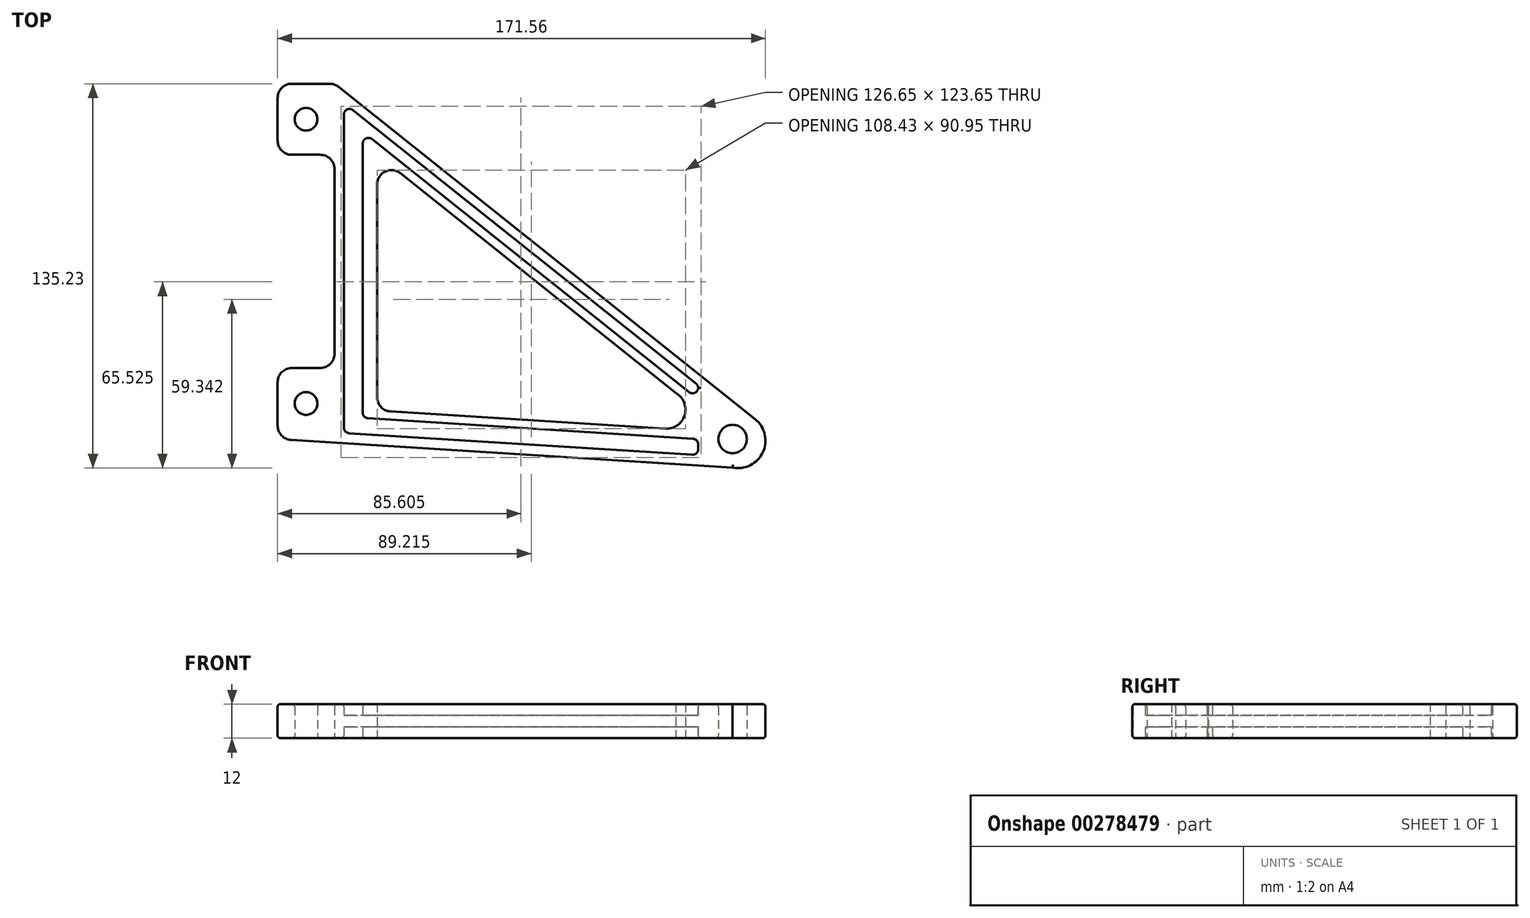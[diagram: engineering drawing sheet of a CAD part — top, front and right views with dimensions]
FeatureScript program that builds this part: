
annotation { "Feature Type Name" : "Feature", "Feature Type Description" : "" }
export const myFeature = defineFeature(function(context is Context, id is Id, definition is map)
    precondition{}
    {
        {
            var Q0;
            Q0=qCreatedBy(makeId("Top.planeOp"),FACE);
            var sketch = newSketch(context, id + "F0", { "sketchPlane" : qUnion([Q0])});
            skCircle(sketch, "E0", {"center": v(0, 0) * mm, "radius": 5 * mm});
            skCircle(sketch, "E1", {"center": v(-150, 12.5) * mm, "radius": 4 * mm});
            skCircle(sketch, "E2", {"center": v(-150, 112.5) * mm, "radius": 4 * mm});
            skLineSegment(sketch, "E3", {"start": v(0, -10.05) * mm, "end": v(-160, 0) * mm});
            skLineSegment(sketch, "E4", {"start": v(-160, 0) * mm, "end": v(-160, 25) * mm});
            skLineSegment(sketch, "E5", {"start": v(-160, 25) * mm, "end": v(-140, 25) * mm});
            skLineSegment(sketch, "E6", {"start": v(-140, 25) * mm, "end": v(-140, 100) * mm});
            skLineSegment(sketch, "E7", {"start": v(-140, 100) * mm, "end": v(-160, 100) * mm});
            skLineSegment(sketch, "E8", {"start": v(-160, 100) * mm, "end": v(-160, 125) * mm});
            skLineSegment(sketch, "E9", {"start": v(-125, 100) * mm, "end": v(-125, 10) * mm});
            skLineSegment(sketch, "E10", {"start": v(-125, 10) * mm, "end": v(-23.73, 3.64) * mm});
            skLineSegment(sketch, "E11", {"start": v(-20.03, 16.27) * mm, "end": v(-125, 100) * mm});
            skLineSegment(sketch, "E12", {"start": v(-160, 125) * mm, "end": v(-140, 125) * mm});
            skLineSegment(sketch, "E13", {"start": v(-140, 125) * mm, "end": v(7.92, 7.02) * mm});
            skArc(sketch, "E14", {"start": v(7.92, 7.02) * mm, "mid": v(10.66, -4.62) * mm, "end": v(0, -10.05) * mm});
            skArc(sketch, "E15", {"start": v(-23.73, 3.64) * mm, "mid": v(-16.83, 8.47) * mm, "end": v(-20.03, 16.27) * mm});
            skLineSegment(sketch, "E16", {"start": v(-136.72, 113) * mm, "end": v(-136.72, 2.16) * mm});
            skLineSegment(sketch, "E17", {"start": v(-136.72, 2.16) * mm, "end": v(-12.07, -5.67) * mm});
            skLineSegment(sketch, "E18", {"start": v(-12.07, -5.67) * mm, "end": v(-12.07, 0) * mm});
            skLineSegment(sketch, "E19", {"start": v(-12.07, 0) * mm, "end": v(-130.08, 7.41) * mm});
            skLineSegment(sketch, "E20", {"start": v(-130.08, 7.41) * mm, "end": v(-130.08, 108.08) * mm});
            skLineSegment(sketch, "E21", {"start": v(-130.08, 108.08) * mm, "end": v(-12.07, 13.96) * mm});
            skLineSegment(sketch, "E22", {"start": v(-12.07, 13.96) * mm, "end": v(-12.07, 18.87) * mm});
            skLineSegment(sketch, "E23", {"start": v(-12.07, 18.87) * mm, "end": v(-136.72, 118.3) * mm});
            skLineSegment(sketch, "E24", {"start": v(-136.72, 118.3) * mm, "end": v(-136.72, 113) * mm});
            skSolve(sketch);
        }
        {
            var Q0;
            Q0=makeQuery(id+"F0.imprint","IMPRINT",FACE,{"disambiguationData":[TD([[makeQuery(id+"F0.imprint","IMPRINT",EDGE,{"derivedFrom":sQuery(id+"F0.wireOp",EDGE,"E0")}),-1.0]])]});
            extrude(context, id + "F1", {"entities" : qUnion([Q0]), "depth" : 12 * mm});
        }
        {
            var Q0;
            Q0=makeQuery(id+"F1.opExtrude","SWEPT_EDGE",EDGE,{"disambiguationData":[OSD([sQuery(id+"F0.wireOp",EDGE,"E5"),sQuery(id+"F0.wireOp",EDGE,"E6")])]});
            var Q1;
            Q1=makeQuery(id+"F1.opExtrude","SWEPT_EDGE",EDGE,{"disambiguationData":[OSD([sQuery(id+"F0.wireOp",EDGE,"E6"),sQuery(id+"F0.wireOp",EDGE,"E7")])]});
            var Q2;
            Q2=makeQuery(id+"F1.opExtrude","SWEPT_EDGE",EDGE,{"disambiguationData":[OSD([sQuery(id+"F0.wireOp",EDGE,"E9"),sQuery(id+"F0.wireOp",EDGE,"E10")])]});
            var Q3;
            Q3=makeQuery(id+"F1.opExtrude","SWEPT_EDGE",EDGE,{"disambiguationData":[OSD([sQuery(id+"F0.wireOp",EDGE,"E9"),sQuery(id+"F0.wireOp",EDGE,"E11")])]});
            var Q4;
            Q4=makeQuery(id+"F1.opExtrude","SWEPT_EDGE",EDGE,{"disambiguationData":[OSD([sQuery(id+"F0.wireOp",EDGE,"E4"),sQuery(id+"F0.wireOp",EDGE,"E5")])]});
            var Q5;
            Q5=makeQuery(id+"F1.opExtrude","SWEPT_EDGE",EDGE,{"disambiguationData":[OSD([sQuery(id+"F0.wireOp",EDGE,"E3"),sQuery(id+"F0.wireOp",EDGE,"E4")])]});
            var Q6;
            Q6=makeQuery(id+"F1.opExtrude","SWEPT_EDGE",EDGE,{"disambiguationData":[OSD([sQuery(id+"F0.wireOp",EDGE,"E7"),sQuery(id+"F0.wireOp",EDGE,"E8")])]});
            var Q7;
            Q7=makeQuery(id+"F1.opExtrude","SWEPT_EDGE",EDGE,{"disambiguationData":[OSD([sQuery(id+"F0.wireOp",EDGE,"E8"),sQuery(id+"F0.wireOp",EDGE,"E12")])]});
            var Q8;
            Q8=makeQuery(id+"F1.opExtrude","SWEPT_EDGE",EDGE,{"disambiguationData":[OSD([sQuery(id+"F0.wireOp",EDGE,"E12"),sQuery(id+"F0.wireOp",EDGE,"E13")])]});
            fillet(context, id + "F2", {"entities" : qUnion([Q0, Q1, Q2, Q3, Q4, Q5, Q6, Q7, Q8]), "radius" : 5 * mm, "tangentPropagation" : true, "allowEdgeOverflow" : false});
        }
        {
            var Q0;
            Q0=makeQuery(id+"F0.imprint","IMPRINT",FACE,{"disambiguationData":[TD([[makeQuery(id+"F0.imprint","IMPRINT",EDGE,{"derivedFrom":sQuery(id+"F0.wireOp",EDGE,"E16")}),1.0]])]});
            extrude(context, id + "F3", {"entities" : qUnion([Q0]), "operationType" : NewBodyOperationType.ADD, "depth" : 8 * mm, "hasSecondDirection" : true, "secondDirectionOppositeDirection" : false, "secondDirectionDepth" : 4 * mm});
        }
        {
            var Q0;
            {var subQ0=sQuery(id+"F0.wireOp",EDGE,"E24");var subQ1=sQuery(id+"F0.wireOp",EDGE,"E23");var subQ2=sQuery(id+"F0.wireOp",EDGE,"E22");var subQ3=sQuery(id+"F0.wireOp",EDGE,"E21");var subQ4=sQuery(id+"F0.wireOp",EDGE,"E20");var subQ5=sQuery(id+"F0.wireOp",EDGE,"E19");var subQ6=sQuery(id+"F0.wireOp",EDGE,"E18");var subQ7=sQuery(id+"F0.wireOp",EDGE,"E17");var subQ8=sQuery(id+"F0.wireOp",EDGE,"E16");Q0=makeQuery(id+"F3.boolean.opBoolean","SPLIT",EDGE,{"disambiguationData":[TD([makeQuery(id+"F3.opExtrude","CAP_FACE",FACE,{"disambiguationData":[OSD([subQ8,subQ7,subQ6,subQ5,subQ4,subQ3,subQ2,subQ1,subQ0])],"isStart":false})])],"derivedFrom":makeQuery(id+"F1.opExtrude","SWEPT_EDGE",EDGE,{"disambiguationData":[OSD([subQ1,subQ0])]})});}
            var Q1;
            {var subQ0=sQuery(id+"F0.wireOp",EDGE,"E24");var subQ1=sQuery(id+"F0.wireOp",EDGE,"E23");var subQ2=sQuery(id+"F0.wireOp",EDGE,"E22");var subQ3=sQuery(id+"F0.wireOp",EDGE,"E21");var subQ4=sQuery(id+"F0.wireOp",EDGE,"E20");var subQ5=sQuery(id+"F0.wireOp",EDGE,"E19");var subQ6=sQuery(id+"F0.wireOp",EDGE,"E18");var subQ7=sQuery(id+"F0.wireOp",EDGE,"E17");var subQ8=sQuery(id+"F0.wireOp",EDGE,"E16");Q1=makeQuery(id+"F3.boolean.opBoolean","SPLIT",EDGE,{"disambiguationData":[TD([makeQuery(id+"F3.opExtrude","CAP_FACE",FACE,{"disambiguationData":[OSD([subQ8,subQ7,subQ6,subQ5,subQ4,subQ3,subQ2,subQ1,subQ0])],"isStart":false})])],"derivedFrom":makeQuery(id+"F1.opExtrude","SWEPT_EDGE",EDGE,{"disambiguationData":[OSD([subQ5,subQ4])]})});}
            var Q2;
            {var subQ0=sQuery(id+"F0.wireOp",EDGE,"E24");var subQ1=sQuery(id+"F0.wireOp",EDGE,"E23");var subQ2=sQuery(id+"F0.wireOp",EDGE,"E22");var subQ3=sQuery(id+"F0.wireOp",EDGE,"E21");var subQ4=sQuery(id+"F0.wireOp",EDGE,"E20");var subQ5=sQuery(id+"F0.wireOp",EDGE,"E19");var subQ6=sQuery(id+"F0.wireOp",EDGE,"E18");var subQ7=sQuery(id+"F0.wireOp",EDGE,"E17");var subQ8=sQuery(id+"F0.wireOp",EDGE,"E16");Q2=makeQuery(id+"F3.boolean.opBoolean","SPLIT",EDGE,{"disambiguationData":[TD([makeQuery(id+"F3.opExtrude","CAP_FACE",FACE,{"disambiguationData":[OSD([subQ8,subQ7,subQ6,subQ5,subQ4,subQ3,subQ2,subQ1,subQ0])],"isStart":false})])],"derivedFrom":makeQuery(id+"F1.opExtrude","SWEPT_EDGE",EDGE,{"disambiguationData":[OSD([subQ8,subQ7])]})});}
            var Q3;
            {var subQ0=sQuery(id+"F0.wireOp",EDGE,"E24");var subQ1=sQuery(id+"F0.wireOp",EDGE,"E23");var subQ2=sQuery(id+"F0.wireOp",EDGE,"E22");var subQ3=sQuery(id+"F0.wireOp",EDGE,"E21");var subQ4=sQuery(id+"F0.wireOp",EDGE,"E20");var subQ5=sQuery(id+"F0.wireOp",EDGE,"E19");var subQ6=sQuery(id+"F0.wireOp",EDGE,"E18");var subQ7=sQuery(id+"F0.wireOp",EDGE,"E17");var subQ8=sQuery(id+"F0.wireOp",EDGE,"E16");Q3=makeQuery(id+"F3.boolean.opBoolean","SPLIT",EDGE,{"disambiguationData":[TD([makeQuery(id+"F3.opExtrude","CAP_FACE",FACE,{"disambiguationData":[OSD([subQ8,subQ7,subQ6,subQ5,subQ4,subQ3,subQ2,subQ1,subQ0])],"isStart":false})])],"derivedFrom":makeQuery(id+"F1.opExtrude","SWEPT_EDGE",EDGE,{"disambiguationData":[OSD([subQ4,subQ3])]})});}
            var Q4;
            {var subQ0=sQuery(id+"F0.wireOp",EDGE,"E24");var subQ1=sQuery(id+"F0.wireOp",EDGE,"E23");var subQ2=sQuery(id+"F0.wireOp",EDGE,"E22");var subQ3=sQuery(id+"F0.wireOp",EDGE,"E21");var subQ4=sQuery(id+"F0.wireOp",EDGE,"E20");var subQ5=sQuery(id+"F0.wireOp",EDGE,"E19");var subQ6=sQuery(id+"F0.wireOp",EDGE,"E18");var subQ7=sQuery(id+"F0.wireOp",EDGE,"E17");var subQ8=sQuery(id+"F0.wireOp",EDGE,"E16");Q4=makeQuery(id+"F3.boolean.opBoolean","SPLIT",EDGE,{"disambiguationData":[TD([makeQuery(id+"F3.opExtrude","CAP_FACE",FACE,{"disambiguationData":[OSD([subQ8,subQ7,subQ6,subQ5,subQ4,subQ3,subQ2,subQ1,subQ0])],"isStart":false})])],"derivedFrom":makeQuery(id+"F1.opExtrude","SWEPT_EDGE",EDGE,{"disambiguationData":[OSD([subQ2,subQ1])]})});}
            var Q5;
            {var subQ0=sQuery(id+"F0.wireOp",EDGE,"E24");var subQ1=sQuery(id+"F0.wireOp",EDGE,"E23");var subQ2=sQuery(id+"F0.wireOp",EDGE,"E22");var subQ3=sQuery(id+"F0.wireOp",EDGE,"E21");var subQ4=sQuery(id+"F0.wireOp",EDGE,"E20");var subQ5=sQuery(id+"F0.wireOp",EDGE,"E19");var subQ6=sQuery(id+"F0.wireOp",EDGE,"E18");var subQ7=sQuery(id+"F0.wireOp",EDGE,"E17");var subQ8=sQuery(id+"F0.wireOp",EDGE,"E16");Q5=makeQuery(id+"F3.boolean.opBoolean","SPLIT",EDGE,{"disambiguationData":[TD([makeQuery(id+"F3.opExtrude","CAP_FACE",FACE,{"disambiguationData":[OSD([subQ8,subQ7,subQ6,subQ5,subQ4,subQ3,subQ2,subQ1,subQ0])],"isStart":false})])],"derivedFrom":makeQuery(id+"F1.opExtrude","SWEPT_EDGE",EDGE,{"disambiguationData":[OSD([subQ7,subQ6])]})});}
            var Q6;
            {var subQ0=sQuery(id+"F0.wireOp",EDGE,"E24");var subQ1=sQuery(id+"F0.wireOp",EDGE,"E23");var subQ2=sQuery(id+"F0.wireOp",EDGE,"E22");var subQ3=sQuery(id+"F0.wireOp",EDGE,"E21");var subQ4=sQuery(id+"F0.wireOp",EDGE,"E20");var subQ5=sQuery(id+"F0.wireOp",EDGE,"E19");var subQ6=sQuery(id+"F0.wireOp",EDGE,"E18");var subQ7=sQuery(id+"F0.wireOp",EDGE,"E17");var subQ8=sQuery(id+"F0.wireOp",EDGE,"E16");Q6=makeQuery(id+"F3.boolean.opBoolean","SPLIT",EDGE,{"disambiguationData":[TD([makeQuery(id+"F3.opExtrude","CAP_FACE",FACE,{"disambiguationData":[OSD([subQ8,subQ7,subQ6,subQ5,subQ4,subQ3,subQ2,subQ1,subQ0])],"isStart":false})])],"derivedFrom":makeQuery(id+"F1.opExtrude","SWEPT_EDGE",EDGE,{"disambiguationData":[OSD([subQ6,subQ5])]})});}
            var Q7;
            {var subQ0=sQuery(id+"F0.wireOp",EDGE,"E24");var subQ1=sQuery(id+"F0.wireOp",EDGE,"E23");var subQ2=sQuery(id+"F0.wireOp",EDGE,"E22");var subQ3=sQuery(id+"F0.wireOp",EDGE,"E21");var subQ4=sQuery(id+"F0.wireOp",EDGE,"E20");var subQ5=sQuery(id+"F0.wireOp",EDGE,"E19");var subQ6=sQuery(id+"F0.wireOp",EDGE,"E18");var subQ7=sQuery(id+"F0.wireOp",EDGE,"E17");var subQ8=sQuery(id+"F0.wireOp",EDGE,"E16");Q7=makeQuery(id+"F3.boolean.opBoolean","SPLIT",EDGE,{"disambiguationData":[TD([makeQuery(id+"F3.opExtrude","CAP_FACE",FACE,{"disambiguationData":[OSD([subQ8,subQ7,subQ6,subQ5,subQ4,subQ3,subQ2,subQ1,subQ0])],"isStart":false})])],"derivedFrom":makeQuery(id+"F1.opExtrude","SWEPT_EDGE",EDGE,{"disambiguationData":[OSD([subQ3,subQ2])]})});}
            var Q8;
            {var subQ0=sQuery(id+"F0.wireOp",EDGE,"E24");var subQ1=sQuery(id+"F0.wireOp",EDGE,"E23");var subQ2=sQuery(id+"F0.wireOp",EDGE,"E22");var subQ3=sQuery(id+"F0.wireOp",EDGE,"E21");var subQ4=sQuery(id+"F0.wireOp",EDGE,"E20");var subQ5=sQuery(id+"F0.wireOp",EDGE,"E19");var subQ6=sQuery(id+"F0.wireOp",EDGE,"E18");var subQ7=sQuery(id+"F0.wireOp",EDGE,"E17");var subQ8=sQuery(id+"F0.wireOp",EDGE,"E16");Q8=makeQuery(id+"F3.boolean.opBoolean","SPLIT",EDGE,{"disambiguationData":[TD([makeQuery(id+"F3.opExtrude","CAP_FACE",FACE,{"disambiguationData":[OSD([subQ8,subQ7,subQ6,subQ5,subQ4,subQ3,subQ2,subQ1,subQ0])],"isStart":true})])],"derivedFrom":makeQuery(id+"F1.opExtrude","SWEPT_EDGE",EDGE,{"disambiguationData":[OSD([subQ1,subQ0])]})});}
            var Q9;
            {var subQ0=sQuery(id+"F0.wireOp",EDGE,"E24");var subQ1=sQuery(id+"F0.wireOp",EDGE,"E23");var subQ2=sQuery(id+"F0.wireOp",EDGE,"E22");var subQ3=sQuery(id+"F0.wireOp",EDGE,"E21");var subQ4=sQuery(id+"F0.wireOp",EDGE,"E20");var subQ5=sQuery(id+"F0.wireOp",EDGE,"E19");var subQ6=sQuery(id+"F0.wireOp",EDGE,"E18");var subQ7=sQuery(id+"F0.wireOp",EDGE,"E17");var subQ8=sQuery(id+"F0.wireOp",EDGE,"E16");Q9=makeQuery(id+"F3.boolean.opBoolean","SPLIT",EDGE,{"disambiguationData":[TD([makeQuery(id+"F3.opExtrude","CAP_FACE",FACE,{"disambiguationData":[OSD([subQ8,subQ7,subQ6,subQ5,subQ4,subQ3,subQ2,subQ1,subQ0])],"isStart":true})])],"derivedFrom":makeQuery(id+"F1.opExtrude","SWEPT_EDGE",EDGE,{"disambiguationData":[OSD([subQ4,subQ3])]})});}
            var Q10;
            {var subQ0=sQuery(id+"F0.wireOp",EDGE,"E24");var subQ1=sQuery(id+"F0.wireOp",EDGE,"E23");var subQ2=sQuery(id+"F0.wireOp",EDGE,"E22");var subQ3=sQuery(id+"F0.wireOp",EDGE,"E21");var subQ4=sQuery(id+"F0.wireOp",EDGE,"E20");var subQ5=sQuery(id+"F0.wireOp",EDGE,"E19");var subQ6=sQuery(id+"F0.wireOp",EDGE,"E18");var subQ7=sQuery(id+"F0.wireOp",EDGE,"E17");var subQ8=sQuery(id+"F0.wireOp",EDGE,"E16");Q10=makeQuery(id+"F3.boolean.opBoolean","SPLIT",EDGE,{"disambiguationData":[TD([makeQuery(id+"F3.opExtrude","CAP_FACE",FACE,{"disambiguationData":[OSD([subQ8,subQ7,subQ6,subQ5,subQ4,subQ3,subQ2,subQ1,subQ0])],"isStart":true})])],"derivedFrom":makeQuery(id+"F1.opExtrude","SWEPT_EDGE",EDGE,{"disambiguationData":[OSD([subQ2,subQ1])]})});}
            var Q11;
            {var subQ0=sQuery(id+"F0.wireOp",EDGE,"E24");var subQ1=sQuery(id+"F0.wireOp",EDGE,"E23");var subQ2=sQuery(id+"F0.wireOp",EDGE,"E22");var subQ3=sQuery(id+"F0.wireOp",EDGE,"E21");var subQ4=sQuery(id+"F0.wireOp",EDGE,"E20");var subQ5=sQuery(id+"F0.wireOp",EDGE,"E19");var subQ6=sQuery(id+"F0.wireOp",EDGE,"E18");var subQ7=sQuery(id+"F0.wireOp",EDGE,"E17");var subQ8=sQuery(id+"F0.wireOp",EDGE,"E16");Q11=makeQuery(id+"F3.boolean.opBoolean","SPLIT",EDGE,{"disambiguationData":[TD([makeQuery(id+"F3.opExtrude","CAP_FACE",FACE,{"disambiguationData":[OSD([subQ8,subQ7,subQ6,subQ5,subQ4,subQ3,subQ2,subQ1,subQ0])],"isStart":true})])],"derivedFrom":makeQuery(id+"F1.opExtrude","SWEPT_EDGE",EDGE,{"disambiguationData":[OSD([subQ3,subQ2])]})});}
            var Q12;
            {var subQ0=sQuery(id+"F0.wireOp",EDGE,"E24");var subQ1=sQuery(id+"F0.wireOp",EDGE,"E23");var subQ2=sQuery(id+"F0.wireOp",EDGE,"E22");var subQ3=sQuery(id+"F0.wireOp",EDGE,"E21");var subQ4=sQuery(id+"F0.wireOp",EDGE,"E20");var subQ5=sQuery(id+"F0.wireOp",EDGE,"E19");var subQ6=sQuery(id+"F0.wireOp",EDGE,"E18");var subQ7=sQuery(id+"F0.wireOp",EDGE,"E17");var subQ8=sQuery(id+"F0.wireOp",EDGE,"E16");Q12=makeQuery(id+"F3.boolean.opBoolean","SPLIT",EDGE,{"disambiguationData":[TD([makeQuery(id+"F3.opExtrude","CAP_FACE",FACE,{"disambiguationData":[OSD([subQ8,subQ7,subQ6,subQ5,subQ4,subQ3,subQ2,subQ1,subQ0])],"isStart":true})])],"derivedFrom":makeQuery(id+"F1.opExtrude","SWEPT_EDGE",EDGE,{"disambiguationData":[OSD([subQ6,subQ5])]})});}
            var Q13;
            {var subQ0=sQuery(id+"F0.wireOp",EDGE,"E24");var subQ1=sQuery(id+"F0.wireOp",EDGE,"E23");var subQ2=sQuery(id+"F0.wireOp",EDGE,"E22");var subQ3=sQuery(id+"F0.wireOp",EDGE,"E21");var subQ4=sQuery(id+"F0.wireOp",EDGE,"E20");var subQ5=sQuery(id+"F0.wireOp",EDGE,"E19");var subQ6=sQuery(id+"F0.wireOp",EDGE,"E18");var subQ7=sQuery(id+"F0.wireOp",EDGE,"E17");var subQ8=sQuery(id+"F0.wireOp",EDGE,"E16");Q13=makeQuery(id+"F3.boolean.opBoolean","SPLIT",EDGE,{"disambiguationData":[TD([makeQuery(id+"F3.opExtrude","CAP_FACE",FACE,{"disambiguationData":[OSD([subQ8,subQ7,subQ6,subQ5,subQ4,subQ3,subQ2,subQ1,subQ0])],"isStart":true})])],"derivedFrom":makeQuery(id+"F1.opExtrude","SWEPT_EDGE",EDGE,{"disambiguationData":[OSD([subQ7,subQ6])]})});}
            var Q14;
            {var subQ0=sQuery(id+"F0.wireOp",EDGE,"E24");var subQ1=sQuery(id+"F0.wireOp",EDGE,"E23");var subQ2=sQuery(id+"F0.wireOp",EDGE,"E22");var subQ3=sQuery(id+"F0.wireOp",EDGE,"E21");var subQ4=sQuery(id+"F0.wireOp",EDGE,"E20");var subQ5=sQuery(id+"F0.wireOp",EDGE,"E19");var subQ6=sQuery(id+"F0.wireOp",EDGE,"E18");var subQ7=sQuery(id+"F0.wireOp",EDGE,"E17");var subQ8=sQuery(id+"F0.wireOp",EDGE,"E16");Q14=makeQuery(id+"F3.boolean.opBoolean","SPLIT",EDGE,{"disambiguationData":[TD([makeQuery(id+"F3.opExtrude","CAP_FACE",FACE,{"disambiguationData":[OSD([subQ8,subQ7,subQ6,subQ5,subQ4,subQ3,subQ2,subQ1,subQ0])],"isStart":true})])],"derivedFrom":makeQuery(id+"F1.opExtrude","SWEPT_EDGE",EDGE,{"disambiguationData":[OSD([subQ5,subQ4])]})});}
            var Q15;
            {var subQ0=sQuery(id+"F0.wireOp",EDGE,"E24");var subQ1=sQuery(id+"F0.wireOp",EDGE,"E23");var subQ2=sQuery(id+"F0.wireOp",EDGE,"E22");var subQ3=sQuery(id+"F0.wireOp",EDGE,"E21");var subQ4=sQuery(id+"F0.wireOp",EDGE,"E20");var subQ5=sQuery(id+"F0.wireOp",EDGE,"E19");var subQ6=sQuery(id+"F0.wireOp",EDGE,"E18");var subQ7=sQuery(id+"F0.wireOp",EDGE,"E17");var subQ8=sQuery(id+"F0.wireOp",EDGE,"E16");Q15=makeQuery(id+"F3.boolean.opBoolean","SPLIT",EDGE,{"disambiguationData":[TD([makeQuery(id+"F3.opExtrude","CAP_FACE",FACE,{"disambiguationData":[OSD([subQ8,subQ7,subQ6,subQ5,subQ4,subQ3,subQ2,subQ1,subQ0])],"isStart":true})])],"derivedFrom":makeQuery(id+"F1.opExtrude","SWEPT_EDGE",EDGE,{"disambiguationData":[OSD([subQ8,subQ7])]})});}
            fillet(context, id + "F4", {"entities" : qUnion([Q0, Q1, Q2, Q3, Q4, Q5, Q6, Q7, Q8, Q9, Q10, Q11, Q12, Q13, Q14, Q15]), "radius" : 2 * mm, "tangentPropagation" : true, "allowEdgeOverflow" : false});
        }
        {
            var Q0;
            Q0=makeQuery(id+"F1.opExtrude","CAP_EDGE",EDGE,{"disambiguationData":[OSD([sQuery(id+"F0.wireOp",EDGE,"E23")])],"isStart":true});
            var Q1;
            Q1=makeQuery(id+"F1.opExtrude","CAP_EDGE",EDGE,{"disambiguationData":[OSD([sQuery(id+"F0.wireOp",EDGE,"E17")])],"isStart":false});
            var Q2;
            Q2=makeQuery(id+"F1.opExtrude","CAP_EDGE",EDGE,{"disambiguationData":[OSD([sQuery(id+"F0.wireOp",EDGE,"E13")])],"isStart":false});
            var Q3;
            Q3=makeQuery(id+"F1.opExtrude","CAP_EDGE",EDGE,{"disambiguationData":[OSD([sQuery(id+"F0.wireOp",EDGE,"E13")])],"isStart":true});
            var Q4;
            Q4=makeQuery(id+"F1.opExtrude","CAP_EDGE",EDGE,{"disambiguationData":[OSD([sQuery(id+"F0.wireOp",EDGE,"E2")])],"isStart":true});
            var Q5;
            Q5=makeQuery(id+"F1.opExtrude","CAP_EDGE",EDGE,{"disambiguationData":[OSD([sQuery(id+"F0.wireOp",EDGE,"E2")])],"isStart":false});
            var Q6;
            Q6=makeQuery(id+"F1.opExtrude","CAP_EDGE",EDGE,{"disambiguationData":[OSD([sQuery(id+"F0.wireOp",EDGE,"E1")])],"isStart":false});
            var Q7;
            Q7=makeQuery(id+"F1.opExtrude","CAP_EDGE",EDGE,{"disambiguationData":[OSD([sQuery(id+"F0.wireOp",EDGE,"E1")])],"isStart":true});
            var Q8;
            Q8=makeQuery(id+"F1.opExtrude","CAP_EDGE",EDGE,{"disambiguationData":[OSD([sQuery(id+"F0.wireOp",EDGE,"E0")])],"isStart":true});
            var Q9;
            Q9=makeQuery(id+"F1.opExtrude","CAP_EDGE",EDGE,{"disambiguationData":[OSD([sQuery(id+"F0.wireOp",EDGE,"E0")])],"isStart":false});
            fillet(context, id + "F5", {"entities" : qUnion([Q0, Q1, Q2, Q3, Q4, Q5, Q6, Q7, Q8, Q9]), "radius" : 1 * mm, "tangentPropagation" : true, "allowEdgeOverflow" : false});
        }
    });
